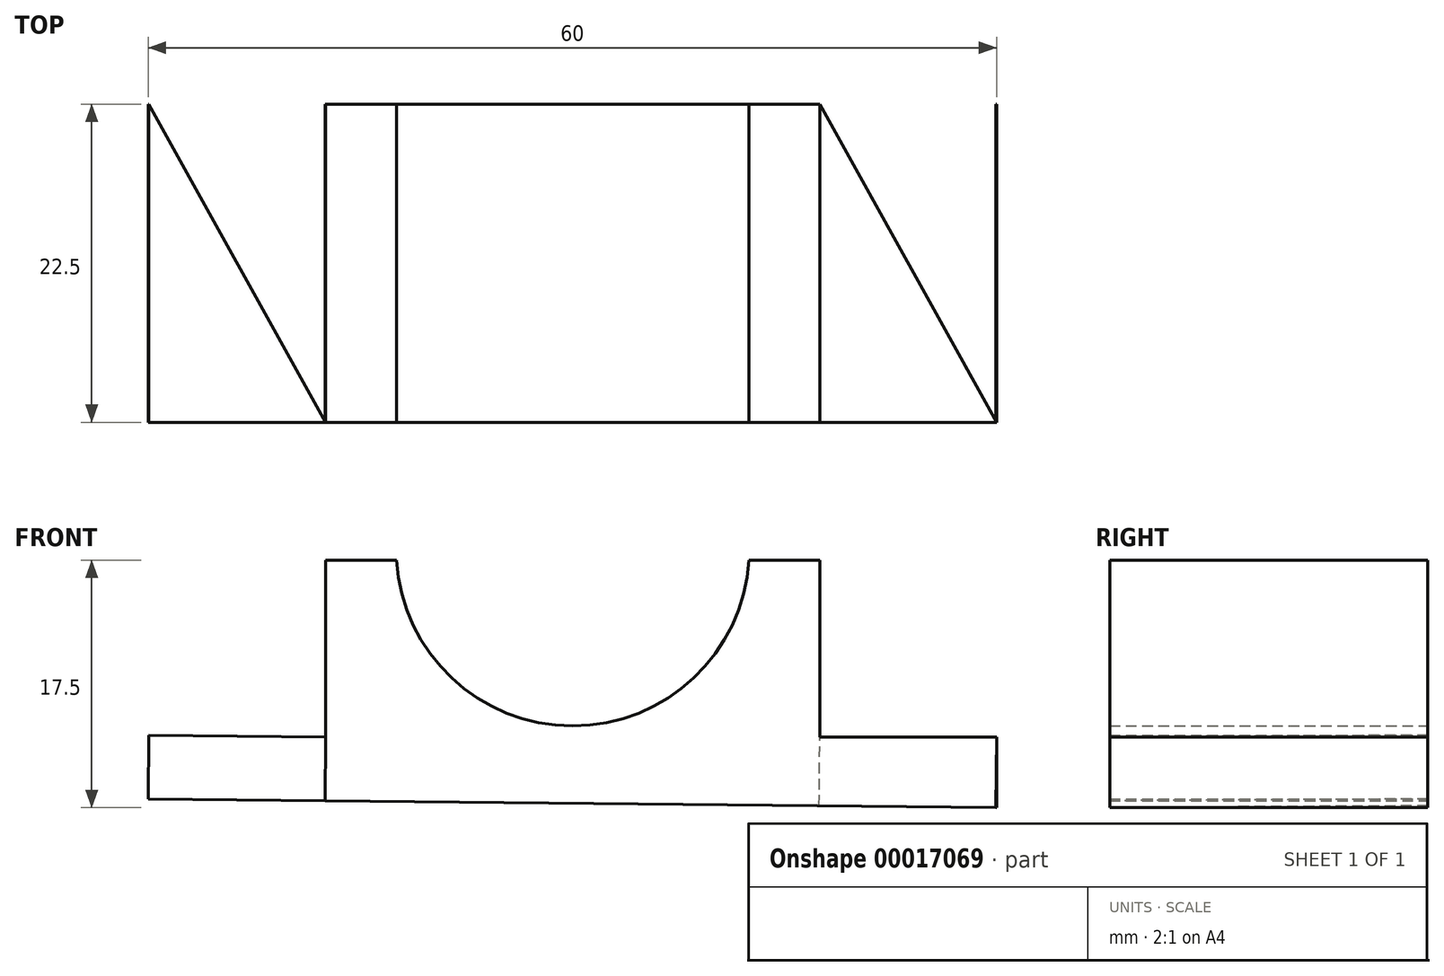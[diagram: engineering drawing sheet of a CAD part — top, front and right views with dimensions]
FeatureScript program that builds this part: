
annotation { "Feature Type Name" : "Feature", "Feature Type Description" : "" }
export const myFeature = defineFeature(function(context is Context, id is Id, definition is map)
    precondition{}
    {
        {
            var Q0;
            Q0=qCreatedBy(makeId("Front.planeOp"),FACE);
            var sketch = newSketch(context, id + "F0", { "sketchPlane" : qUnion([Q0])});
            skLineSegment(sketch, "E0", {"start": v(-27.93, -12.92) * mm, "end": v(-27.98, -17.43) * mm});
            skLineSegment(sketch, "E1", {"start": v(-27.93, -12.92) * mm, "end": v(-15.43, -13.04) * mm});
            skLineSegment(sketch, "E2", {"start": v(-15.43, -13.04) * mm, "end": v(-15.43, -0.54) * mm});
            skLineSegment(sketch, "E3", {"start": v(-15.43, -0.54) * mm, "end": v(-10.43, -0.54) * mm});
            skLineSegment(sketch, "E4", {"start": v(-27.98, -17.43) * mm, "end": v(32.02, -18.04) * mm});
            skLineSegment(sketch, "E5", {"start": v(32.02, -18.04) * mm, "end": v(32.02, -13.04) * mm});
            skLineSegment(sketch, "E6", {"start": v(32.02, -13.04) * mm, "end": v(19.52, -13.04) * mm});
            skLineSegment(sketch, "E7", {"start": v(19.52, -13.04) * mm, "end": v(19.52, -0.54) * mm});
            skLineSegment(sketch, "E8", {"start": v(14.52, -0.54) * mm, "end": v(19.52, -0.54) * mm});
            skArc(sketch, "E9", {"start": v(-10.43, -0.54) * mm, "mid": v(2.04, -12.27) * mm, "end": v(14.52, -0.54) * mm});
            skSolve(sketch);
        }
        {
            var Q0;
            Q0 = qSketchRegion(id + "F0", true);
            extrude(context, id + "F1", {"entities" : qUnion([Q0]), "depth" : 22.5 * mm});
        }
        {
            var Q0;
            Q0=makeQuery(id+"F1.opExtrude","SWEPT_FACE",FACE,{"disambiguationData":[OSD([sQuery(id+"F0.wireOp",EDGE,"E6")])]});
            var sketch = newSketch(context, id + "F2", { "sketchPlane" : qUnion([Q0])});
            skLineSegment(sketch, "E10", {"start": v(19.52, -22.5) * mm, "end": v(32.02, 0) * mm});
            skLineSegment(sketch, "E11", {"start": v(32.02, 0) * mm, "end": v(19.52, 0) * mm});
            skLineSegment(sketch, "E12", {"start": v(19.52, 0) * mm, "end": v(32.02, -22.5) * mm});
            skCircle(sketch, "E13", {"center": v(25.77, -11.25) * mm, "radius": 2.5 * mm});
            skSolve(sketch);
        }
        {
            var Q0;
            Q0=makeQuery(id+"F1.opExtrude","SWEPT_FACE",FACE,{"disambiguationData":[OSD([sQuery(id+"F0.wireOp",EDGE,"E1")])]});
            var sketch = newSketch(context, id + "F3", { "sketchPlane" : qUnion([Q0])});
            skLineSegment(sketch, "E14", {"start": v(-27.8, -22.5) * mm, "end": v(-15.3, 0) * mm});
            skLineSegment(sketch, "E15", {"start": v(-15.3, 0) * mm, "end": v(-27.8, 0) * mm});
            skLineSegment(sketch, "E16", {"start": v(-27.8, 0) * mm, "end": v(-15.3, -22.5) * mm});
            skCircle(sketch, "E17", {"center": v(-21.55, -11.25) * mm, "radius": 2.5 * mm});
            skSolve(sketch);
        }
        {
            var Q0;
            {var subQ1=sQuery(id+"F3.wireOp",EDGE,"E16");var subQ3=sQuery(id+"F3.wireOp",EDGE,"E14");var subQ5=makeQuery(id+"F3.imprint","INTERSECT",VERTEX,{"derivedFrom":[subQ3,subQ1]});Q0=makeQuery(id+"F3.imprint","IMPRINT",FACE,{"disambiguationData":[TD([[makeQuery(id+"F3.imprint","IMPRINT",EDGE,{"disambiguationData":[TD([[subQ5,-1.0]])],"derivedFrom":subQ3}),-1.0]])]});}
            var Q1;
            {var subQ1=sQuery(id+"F3.wireOp",EDGE,"E16");var subQ3=sQuery(id+"F3.wireOp",EDGE,"E14");var subQ5=makeQuery(id+"F3.imprint","INTERSECT",VERTEX,{"derivedFrom":[subQ3,subQ1]});Q1=makeQuery(id+"F3.imprint","IMPRINT",FACE,{"disambiguationData":[TD([[makeQuery(id+"F3.imprint","IMPRINT",EDGE,{"disambiguationData":[TD([[subQ5,-1.0]])],"derivedFrom":subQ3}),1.0]])]});}
            var Q2;
            {var subQ0=sQuery(id+"F3.wireOp",EDGE,"E17");var subQ3=sQuery(id+"F3.wireOp",EDGE,"E14");var subQ4=makeQuery(id+"F3.imprint","INTERSECT",VERTEX,{"disambiguationData":[OD(0.0)],"derivedFrom":[subQ3,subQ0]});Q2=makeQuery(id+"F3.imprint","IMPRINT",FACE,{"disambiguationData":[TD([[makeQuery(id+"F3.imprint","IMPRINT",EDGE,{"disambiguationData":[TD([[subQ4,-1.0]])],"derivedFrom":subQ3}),1.0]])]});}
            var Q3;
            {var subQ0=sQuery(id+"F3.wireOp",EDGE,"E17");var subQ3=sQuery(id+"F3.wireOp",EDGE,"E14");var subQ4=makeQuery(id+"F3.imprint","INTERSECT",VERTEX,{"disambiguationData":[OD(0.0)],"derivedFrom":[subQ3,subQ0]});Q3=makeQuery(id+"F3.imprint","IMPRINT",FACE,{"disambiguationData":[TD([[makeQuery(id+"F3.imprint","IMPRINT",EDGE,{"disambiguationData":[TD([[subQ4,-1.0]])],"derivedFrom":subQ3}),-1.0]])]});}
            var Q4;
            {var subQ1=sQuery(id+"F2.wireOp",EDGE,"E12");var subQ3=sQuery(id+"F2.wireOp",EDGE,"E10");var subQ5=makeQuery(id+"F2.imprint","INTERSECT",VERTEX,{"derivedFrom":[subQ3,subQ1]});Q4=makeQuery(id+"F2.imprint","IMPRINT",FACE,{"disambiguationData":[TD([[makeQuery(id+"F2.imprint","IMPRINT",EDGE,{"disambiguationData":[TD([[subQ5,-1.0]])],"derivedFrom":subQ3}),-1.0]])]});}
            var Q5;
            {var subQ1=sQuery(id+"F2.wireOp",EDGE,"E12");var subQ3=sQuery(id+"F2.wireOp",EDGE,"E10");var subQ5=makeQuery(id+"F2.imprint","INTERSECT",VERTEX,{"derivedFrom":[subQ3,subQ1]});Q5=makeQuery(id+"F2.imprint","IMPRINT",FACE,{"disambiguationData":[TD([[makeQuery(id+"F2.imprint","IMPRINT",EDGE,{"disambiguationData":[TD([[subQ5,-1.0]])],"derivedFrom":subQ3}),1.0]])]});}
            var Q6;
            {var subQ0=sQuery(id+"F2.wireOp",EDGE,"E13");var subQ3=sQuery(id+"F2.wireOp",EDGE,"E10");var subQ4=makeQuery(id+"F2.imprint","INTERSECT",VERTEX,{"disambiguationData":[OD(0.0)],"derivedFrom":[subQ3,subQ0]});Q6=makeQuery(id+"F2.imprint","IMPRINT",FACE,{"disambiguationData":[TD([[makeQuery(id+"F2.imprint","IMPRINT",EDGE,{"disambiguationData":[TD([[subQ4,-1.0]])],"derivedFrom":subQ3}),-1.0]])]});}
            var Q7;
            {var subQ0=sQuery(id+"F2.wireOp",EDGE,"E13");var subQ3=sQuery(id+"F2.wireOp",EDGE,"E10");var subQ4=makeQuery(id+"F2.imprint","INTERSECT",VERTEX,{"disambiguationData":[OD(0.0)],"derivedFrom":[subQ3,subQ0]});Q7=makeQuery(id+"F2.imprint","IMPRINT",FACE,{"disambiguationData":[TD([[makeQuery(id+"F2.imprint","IMPRINT",EDGE,{"disambiguationData":[TD([[subQ4,-1.0]])],"derivedFrom":subQ3}),1.0]])]});}
            extrude(context, id + "F4", {"entities" : qUnion([Q0, Q1, Q2, Q3, Q4, Q5, Q6, Q7]), "operationType" : NewBodyOperationType.REMOVE, "endBound" : BoundingType.THROUGH_ALL, "oppositeDirection" : true, "depth" : 25 * mm});
        }
    });
